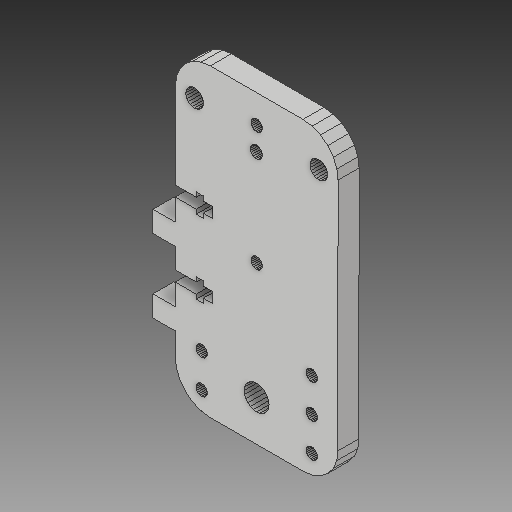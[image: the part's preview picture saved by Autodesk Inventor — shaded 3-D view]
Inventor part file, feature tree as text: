
AUTODESK INVENTOR PART (.ipt)
format: ipt  version: 2018 (Build 220112000, 112)  size: 500,224 bytes
history: native  units: mm
features: extrude x1, sketch x1
ambient origin geometry x8: Origin, YZ Plane, XZ Plane, XY Plane, X Axis, Y Axis, Z Axis, Center Point
bodies: Solid1 (feature_tree)
feature tree (2):
  extrude  "Extrusion1"  [1 undecoded]
  sketch  "Sketch1"  dims[d0=6.0mm d1=0.0mm]
note: 1 required parameter value undecoded (feature->parameter linkage not recoverable at this tier; creation-order binding heuristic only, values carry confidence <= 0.55)
